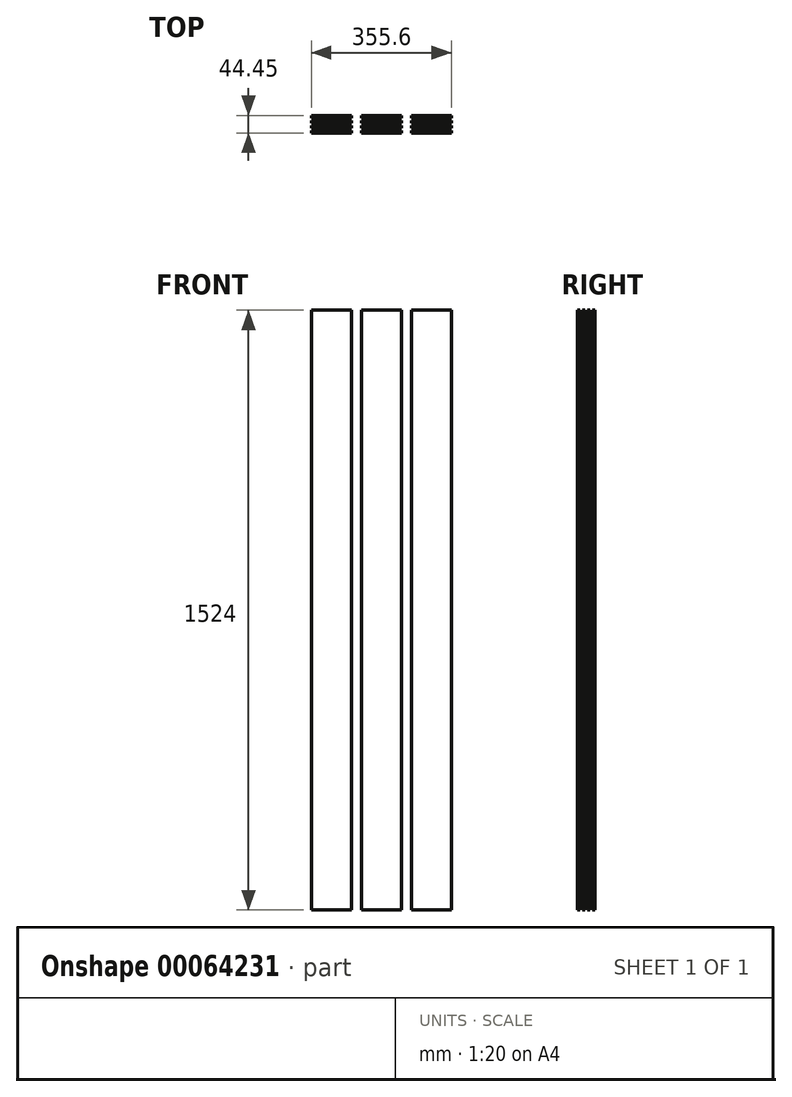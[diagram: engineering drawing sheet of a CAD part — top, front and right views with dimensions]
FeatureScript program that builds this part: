
annotation { "Feature Type Name" : "Feature", "Feature Type Description" : "" }
export const myFeature = defineFeature(function(context is Context, id is Id, definition is map)
    precondition{}
    {
        {
            var Q0;
            Q0=qCreatedBy(makeId("Top.planeOp"),FACE);
            var sketch = newSketch(context, id + "F0", { "sketchPlane" : qUnion([Q0])});
            skLineSegment(sketch, "E0.bottom", {"start": v(0, 0) * mm, "end": v(101.6, 0) * mm});
            skLineSegment(sketch, "E0.top", {"start": v(0, 6.35) * mm, "end": v(101.6, 6.35) * mm});
            skLineSegment(sketch, "E0.left", {"start": v(0, 0) * mm, "end": v(0, 6.35) * mm});
            skLineSegment(sketch, "E0.right", {"start": v(101.6, 0) * mm, "end": v(101.6, 6.35) * mm});
            skLineSegment(sketch, "E1.0.1.0", {"start": v(0, 19.05) * mm, "end": v(101.6, 19.05) * mm});
            skLineSegment(sketch, "E1.0.1.1", {"start": v(0, 12.7) * mm, "end": v(0, 19.05) * mm});
            skLineSegment(sketch, "E1.0.1.2", {"start": v(101.6, 12.7) * mm, "end": v(101.6, 19.05) * mm});
            skLineSegment(sketch, "E1.0.1.3", {"start": v(0, 12.7) * mm, "end": v(101.6, 12.7) * mm});
            skLineSegment(sketch, "E1.0.2.0", {"start": v(0, 31.75) * mm, "end": v(101.6, 31.75) * mm});
            skLineSegment(sketch, "E1.0.2.1", {"start": v(0, 25.4) * mm, "end": v(0, 31.75) * mm});
            skLineSegment(sketch, "E1.0.2.2", {"start": v(101.6, 25.4) * mm, "end": v(101.6, 31.75) * mm});
            skLineSegment(sketch, "E1.0.2.3", {"start": v(0, 25.4) * mm, "end": v(101.6, 25.4) * mm});
            skLineSegment(sketch, "E1.0.3.0", {"start": v(0, 44.45) * mm, "end": v(101.6, 44.45) * mm});
            skLineSegment(sketch, "E1.0.3.1", {"start": v(0, 38.1) * mm, "end": v(0, 44.45) * mm});
            skLineSegment(sketch, "E1.0.3.2", {"start": v(101.6, 38.1) * mm, "end": v(101.6, 44.45) * mm});
            skLineSegment(sketch, "E1.0.3.3", {"start": v(0, 38.1) * mm, "end": v(101.6, 38.1) * mm});
            skLineSegment(sketch, "E1.1.0.0", {"start": v(127, 6.35) * mm, "end": v(228.6, 6.35) * mm});
            skLineSegment(sketch, "E1.1.0.1", {"start": v(127, 0) * mm, "end": v(127, 6.35) * mm});
            skLineSegment(sketch, "E1.1.0.2", {"start": v(228.6, 0) * mm, "end": v(228.6, 6.35) * mm});
            skLineSegment(sketch, "E1.1.0.3", {"start": v(127, 0) * mm, "end": v(228.6, 0) * mm});
            skLineSegment(sketch, "E1.1.1.0", {"start": v(127, 19.05) * mm, "end": v(228.6, 19.05) * mm});
            skLineSegment(sketch, "E1.1.1.1", {"start": v(127, 12.7) * mm, "end": v(127, 19.05) * mm});
            skLineSegment(sketch, "E1.1.1.2", {"start": v(228.6, 12.7) * mm, "end": v(228.6, 19.05) * mm});
            skLineSegment(sketch, "E1.1.1.3", {"start": v(127, 12.7) * mm, "end": v(228.6, 12.7) * mm});
            skLineSegment(sketch, "E1.1.2.0", {"start": v(127, 31.75) * mm, "end": v(228.6, 31.75) * mm});
            skLineSegment(sketch, "E1.1.2.1", {"start": v(127, 25.4) * mm, "end": v(127, 31.75) * mm});
            skLineSegment(sketch, "E1.1.2.2", {"start": v(228.6, 25.4) * mm, "end": v(228.6, 31.75) * mm});
            skLineSegment(sketch, "E1.1.2.3", {"start": v(127, 25.4) * mm, "end": v(228.6, 25.4) * mm});
            skLineSegment(sketch, "E1.1.3.0", {"start": v(127, 44.45) * mm, "end": v(228.6, 44.45) * mm});
            skLineSegment(sketch, "E1.1.3.1", {"start": v(127, 38.1) * mm, "end": v(127, 44.45) * mm});
            skLineSegment(sketch, "E1.1.3.2", {"start": v(228.6, 38.1) * mm, "end": v(228.6, 44.45) * mm});
            skLineSegment(sketch, "E1.1.3.3", {"start": v(127, 38.1) * mm, "end": v(228.6, 38.1) * mm});
            skLineSegment(sketch, "E1.2.0.0", {"start": v(254, 6.35) * mm, "end": v(355.6, 6.35) * mm});
            skLineSegment(sketch, "E1.2.0.1", {"start": v(254, 0) * mm, "end": v(254, 6.35) * mm});
            skLineSegment(sketch, "E1.2.0.2", {"start": v(355.6, 0) * mm, "end": v(355.6, 6.35) * mm});
            skLineSegment(sketch, "E1.2.0.3", {"start": v(254, 0) * mm, "end": v(355.6, 0) * mm});
            skLineSegment(sketch, "E1.2.1.0", {"start": v(254, 19.05) * mm, "end": v(355.6, 19.05) * mm});
            skLineSegment(sketch, "E1.2.1.1", {"start": v(254, 12.7) * mm, "end": v(254, 19.05) * mm});
            skLineSegment(sketch, "E1.2.1.2", {"start": v(355.6, 12.7) * mm, "end": v(355.6, 19.05) * mm});
            skLineSegment(sketch, "E1.2.1.3", {"start": v(254, 12.7) * mm, "end": v(355.6, 12.7) * mm});
            skLineSegment(sketch, "E1.2.2.0", {"start": v(254, 31.75) * mm, "end": v(355.6, 31.75) * mm});
            skLineSegment(sketch, "E1.2.2.1", {"start": v(254, 25.4) * mm, "end": v(254, 31.75) * mm});
            skLineSegment(sketch, "E1.2.2.2", {"start": v(355.6, 25.4) * mm, "end": v(355.6, 31.75) * mm});
            skLineSegment(sketch, "E1.2.2.3", {"start": v(254, 25.4) * mm, "end": v(355.6, 25.4) * mm});
            skLineSegment(sketch, "E1.2.3.0", {"start": v(254, 44.45) * mm, "end": v(355.6, 44.45) * mm});
            skLineSegment(sketch, "E1.2.3.1", {"start": v(254, 38.1) * mm, "end": v(254, 44.45) * mm});
            skLineSegment(sketch, "E1.2.3.2", {"start": v(355.6, 38.1) * mm, "end": v(355.6, 44.45) * mm});
            skLineSegment(sketch, "E1.2.3.3", {"start": v(254, 38.1) * mm, "end": v(355.6, 38.1) * mm});
            skLineSegment(sketch, "E1.direction1", {"start": v(0, 6.35) * mm, "end": v(127, 6.35) * mm, "construction": true});
            skLineSegment(sketch, "E1.direction2", {"start": v(0, 6.35) * mm, "end": v(0, 19.05) * mm, "construction": true});
            skSolve(sketch);
        }
        {
            var Q0;
            Q0=qSketchRegion(id+"F0",true);
            extrude(context, id + "F1", {"entities" : qUnion([Q0]), "endBound" : BoundingType.SYMMETRIC, "depth" : 1524 * mm});
        }
    });
